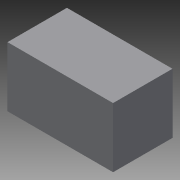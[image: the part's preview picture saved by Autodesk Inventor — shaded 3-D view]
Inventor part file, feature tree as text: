
AUTODESK INVENTOR PART (.ipt)
format: ipt  version: 2013 (Build 170138000, 138)  size: 67,072 bytes
history: native  units: mm
features: extrude x1, sketch x1
ambient origin geometry x8: Origin, YZ Plane, XZ Plane, XY Plane, X Axis, Y Axis, Z Axis, Center Point
bodies: Solid1 (feature_tree)
feature tree (2):
  extrude  "Extrusion1"  Depth=27.5mm
  sketch  "Sketch1"  dims[d0=48.5mm d1=27.5mm d2=27.3mm d3=0.0mm]
